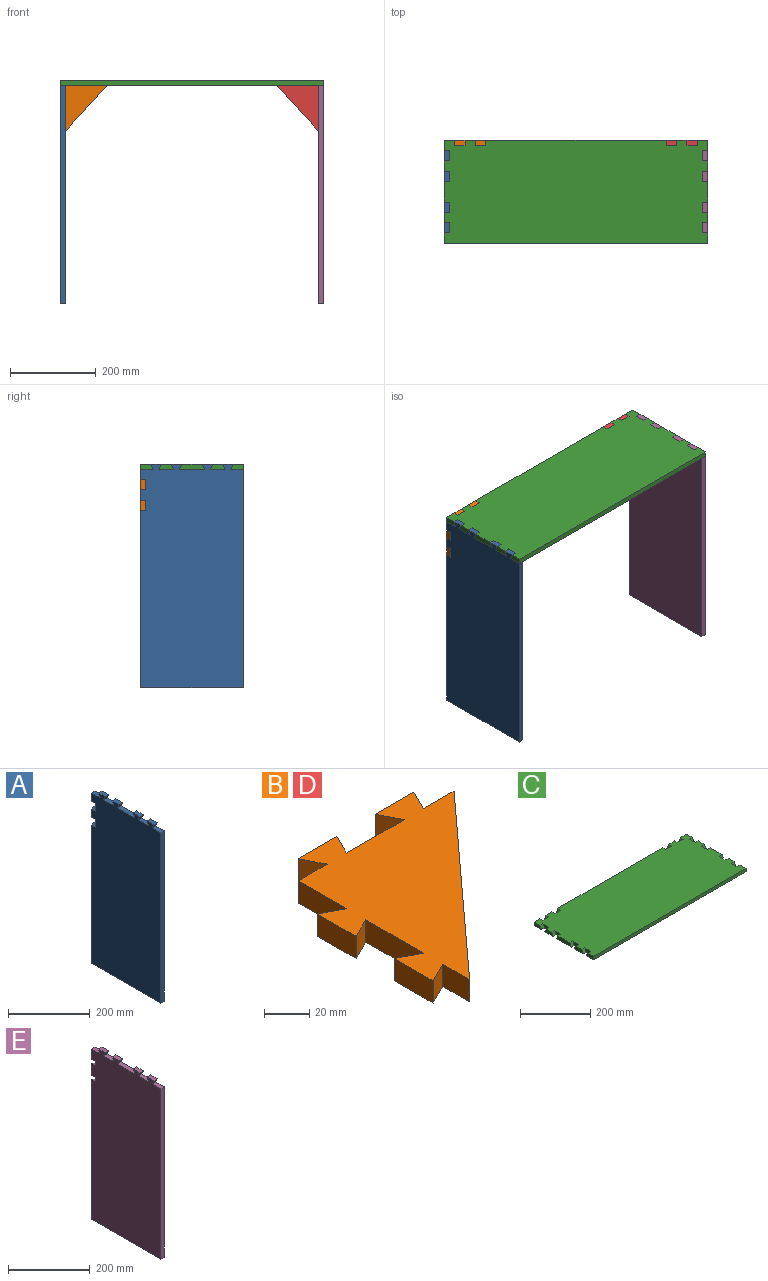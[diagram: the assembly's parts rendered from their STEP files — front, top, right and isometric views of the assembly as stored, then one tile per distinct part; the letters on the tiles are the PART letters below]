
ASSEMBLY  parts=5 mates=4
PART A: 30 faces, bbox 12x240x522 mm
  f0: plane 24x12mm, normal (0,1,0), area 216mm2, adj f24,f25,f28,f29
  f1: plane 24x12mm, normal (0,1,0), area 216mm2, adj f24,f25,f26,f27
  f2: plane 36x12mm, normal (0,0,1), area 432mm2, adj f3,f23,f24,f25
  f3: plane 12x12mm, normal (0,0.89,-0.45), area 161mm2, adj f2,f4,f24,f25
  f4: plane 24x12mm, normal (0,0,1), area 288mm2, adj f3,f5,f24,f25
  f5: plane 12x12mm, normal (0,-0.89,-0.45), area 161mm2, adj f4,f6,f24,f25
  f6: plane 30x12mm, normal (0,0,1), area 360mm2, adj f5,f7,f24,f25
  f7: plane 510x12mm, normal (0,-1,0), area 6120mm2, adj f6,f8,f24,f25
  f8: plane 240x12mm, normal (0,0,-1), area 2880mm2, adj f7,f9,f24,f25
  f9: plane 420x12mm, normal (0,1,0), area 5004mm2, adj f8,f24,f25,f29
  f10: plane 36x12mm, normal (0,1,0), area 360mm2, adj f24,f25,f27,f28
  f11: plane 30x12mm, normal (0,1,0), area 324mm2, adj f12,f24,f25,f26
  f12: plane 30x12mm, normal (0,0,1), area 360mm2, adj f11,f13,f24,f25
  f13: plane 12x12mm, normal (0,0.89,-0.45), area 161mm2, adj f12,f14,f24,f25
  f14: plane 24x12mm, normal (0,0,1), area 288mm2, adj f13,f15,f24,f25
  f15: plane 12x12mm, normal (0,-0.89,-0.45), area 161mm2, adj f14,f16,f24,f25
  f16: plane 36x12mm, normal (0,0,1), area 432mm2, adj f15,f17,f24,f25
  f17: plane 12x12mm, normal (0,0.89,-0.45), area 161mm2, adj f16,f18,f24,f25
  f18: plane 24x12mm, normal (0,0,1), area 288mm2, adj f17,f19,f24,f25
  f19: plane 12x12mm, normal (0,-0.89,-0.45), area 161mm2, adj f18,f20,f24,f25
  f20: plane 60x12mm, normal (0,0,1), area 720mm2, adj f19,f21,f24,f25
  f21: plane 12x12mm, normal (0,0.89,-0.45), area 161mm2, adj f20,f22,f24,f25
  f22: plane 24x12mm, normal (0,0,1), area 288mm2, adj f21,f23,f24,f25
  f23: plane 12x12mm, normal (0,-0.89,-0.45), area 161mm2, adj f2,f22,f24,f25
  f24: plane 522x240mm, normal (1,0,0), area 122976mm2, adj f0,f1,f2,f3,f4,f5,f6,f7
  f25: plane 522x240mm, normal (-1,0,0), area 122688mm2, adj f0,f1,f2,f3,f4,f5,f6,f7
  f26: plane 12x12mm, normal (-0.45,0,-0.89), area 161mm2, adj f1,f11,f24,f25
  f27: plane 12x12mm, normal (-0.45,0,0.89), area 161mm2, adj f1,f10,f24,f25
  f28: plane 12x12mm, normal (-0.45,0,-0.89), area 161mm2, adj f0,f10,f24,f25
  f29: plane 12x12mm, normal (-0.45,0,0.89), area 161mm2, adj f0,f9,f24,f25
PART B: 21 faces, bbox 109.1x118.8x12 mm
  f0: plane 16.8x12mm, normal (-1,0,0), area 201.6mm2, adj f1,f18,f19,f20
  f1: plane 106.8x97.09mm, normal (0.74,-0.67,0), area 1732mm2, adj f0,f2,f19,f20
  f2: plane 19.09x12mm, normal (0,1,0), area 229.1mm2, adj f1,f3,f19,f20
  f3: plane 12x12mm, normal (0.89,-0.45,0), area 161mm2, adj f2,f4,f19,f20
  f4: plane 24x12mm, normal (0,1,0), area 288mm2, adj f3,f5,f19,f20
  f5: plane 12x12mm, normal (-0.89,-0.45,0), area 161mm2, adj f4,f6,f19,f20
  f6: plane 36x12mm, normal (0,1,0), area 432mm2, adj f5,f7,f19,f20
  f7: plane 12x12mm, normal (0.89,-0.45,0), area 161mm2, adj f6,f8,f19,f20
  f8: plane 24x12mm, normal (0,1,0), area 288mm2, adj f7,f9,f19,f20
  f9: plane 12x12mm, normal (-0.89,-0.45,0), area 161mm2, adj f8,f10,f19,f20
  f10: plane 18x12mm, normal (0,1,0), area 216mm2, adj f9,f11,f19,f20
  f11: plane 30x12mm, normal (-1,0,0), area 360mm2, adj f10,f12,f19,f20
  f12: plane 12x12mm, normal (0.45,0.89,0), area 161mm2, adj f11,f13,f19,f20
  f13: plane 24x12mm, normal (-1,0,0), area 288mm2, adj f12,f14,f19,f20
  f14: plane 12x12mm, normal (0.45,-0.89,0), area 161mm2, adj f13,f15,f19,f20
  f15: plane 36x12mm, normal (-1,0,0), area 432mm2, adj f14,f16,f19,f20
  f16: plane 12x12mm, normal (0.45,0.89,0), area 161mm2, adj f15,f17,f19,f20
  f17: plane 24x12mm, normal (-1,0,0), area 288mm2, adj f16,f18,f19,f20
  f18: plane 12x12mm, normal (0.45,-0.89,0), area 161mm2, adj f0,f17,f19,f20
  f19: plane 118.8x109.09mm, normal (0,0,1), area 6048.7mm2, adj f0,f1,f2,f3,f4,f5,f6,f7
  f20: plane 118.8x109.09mm, normal (0,0,-1), area 6048.7mm2, adj f0,f1,f2,f3,f4,f5,f6,f7
PART C: 54 faces, bbox 614x240x12 mm
  f0: plane 24x12mm, normal (0,1,0), area 216mm2, adj f28,f29,f52,f53
  f1: plane 24x12mm, normal (0,1,0), area 216mm2, adj f28,f29,f50,f51
  f2: plane 24x12mm, normal (0,1,0), area 216mm2, adj f28,f29,f48,f49
  f3: plane 24x12mm, normal (0,1,0), area 216mm2, adj f28,f29,f46,f47
  f4: plane 24x12mm, normal (1,0,0), area 216mm2, adj f28,f29,f44,f45
  f5: plane 24x12mm, normal (1,0,0), area 216mm2, adj f28,f29,f42,f43
  f6: plane 24x12mm, normal (-1,0,0), area 216mm2, adj f28,f29,f32,f33
  f7: plane 24x12mm, normal (-1,0,0), area 216mm2, adj f28,f29,f30,f31
  f8: plane 36x12mm, normal (1,0,0), area 360mm2, adj f28,f29,f43,f44
  f9: plane 30x12mm, normal (1,0,0), area 324mm2, adj f10,f28,f29,f45
  f10: plane 30x12mm, normal (0,1,0), area 324mm2, adj f9,f28,f29,f46
  f11: plane 36x12mm, normal (0,1,0), area 360mm2, adj f28,f29,f47,f48
  f12: plane 434x12mm, normal (0,1,0), area 5136mm2, adj f28,f29,f49,f50
  f13: plane 36x12mm, normal (0,1,0), area 360mm2, adj f28,f29,f51,f52
  f14: plane 30x12mm, normal (0,1,0), area 324mm2, adj f15,f28,f29,f53
  f15: plane 30x12mm, normal (-1,0,0), area 324mm2, adj f14,f28,f29,f36
  f16: plane 24x12mm, normal (-1,0,0), area 216mm2, adj f28,f29,f36,f37
  f17: plane 36x12mm, normal (-1,0,0), area 360mm2, adj f28,f29,f34,f37
  f18: plane 24x12mm, normal (-1,0,0), area 216mm2, adj f28,f29,f34,f35
  f19: plane 60x12mm, normal (-1,0,0), area 648mm2, adj f28,f29,f32,f35
  f20: plane 36x12mm, normal (-1,0,0), area 360mm2, adj f28,f29,f30,f33
  f21: plane 30x12mm, normal (-1,0,0), area 324mm2, adj f22,f28,f29,f31
  f22: plane 614x12mm, normal (0,-1,0), area 7368mm2, adj f21,f23,f28,f29
  f23: plane 30x12mm, normal (1,0,0), area 324mm2, adj f22,f28,f29,f38
  f24: plane 24x12mm, normal (1,0,0), area 216mm2, adj f28,f29,f38,f39
  f25: plane 36x12mm, normal (1,0,0), area 360mm2, adj f28,f29,f39,f40
  f26: plane 24x12mm, normal (1,0,0), area 216mm2, adj f28,f29,f40,f41
  f27: plane 60x12mm, normal (1,0,0), area 648mm2, adj f28,f29,f41,f42
  f28: plane 614x240mm, normal (0,0,1), area 143904mm2, adj f0,f1,f2,f3,f4,f5,f6,f7
  f29: plane 614x240mm, normal (0,0,-1), area 145632mm2, adj f0,f1,f2,f3,f4,f5,f6,f7
  f30: plane 12x12mm, normal (0,-0.89,0.45), area 161mm2, adj f7,f20,f28,f29
  f31: plane 12x12mm, normal (0,0.89,0.45), area 161mm2, adj f7,f21,f28,f29
  f32: plane 12x12mm, normal (0,-0.89,0.45), area 161mm2, adj f6,f19,f28,f29
  f33: plane 12x12mm, normal (0,0.89,0.45), area 161mm2, adj f6,f20,f28,f29
  f34: plane 12x12mm, normal (0,-0.89,0.45), area 161mm2, adj f17,f18,f28,f29
  f35: plane 12x12mm, normal (0,0.89,0.45), area 161mm2, adj f18,f19,f28,f29
  f36: plane 12x12mm, normal (0,-0.89,0.45), area 161mm2, adj f15,f16,f28,f29
  f37: plane 12x12mm, normal (0,0.89,0.45), area 161mm2, adj f16,f17,f28,f29
  f38: plane 12x12mm, normal (0,0.89,0.45), area 161mm2, adj f23,f24,f28,f29
  f39: plane 12x12mm, normal (0,-0.89,0.45), area 161mm2, adj f24,f25,f28,f29
  f40: plane 12x12mm, normal (0,0.89,0.45), area 161mm2, adj f25,f26,f28,f29
  f41: plane 12x12mm, normal (0,-0.89,0.45), area 161mm2, adj f26,f27,f28,f29
  f42: plane 12x12mm, normal (0,0.89,0.45), area 161mm2, adj f5,f27,f28,f29
  f43: plane 12x12mm, normal (0,-0.89,0.45), area 161mm2, adj f5,f8,f28,f29
  f44: plane 12x12mm, normal (0,0.89,0.45), area 161mm2, adj f4,f8,f28,f29
  f45: plane 12x12mm, normal (0,-0.89,0.45), area 161mm2, adj f4,f9,f28,f29
  f46: plane 12x12mm, normal (-0.89,0,0.45), area 161mm2, adj f3,f10,f28,f29
  f47: plane 12x12mm, normal (0.89,0,0.45), area 161mm2, adj f3,f11,f28,f29
  f48: plane 12x12mm, normal (-0.89,0,0.45), area 161mm2, adj f2,f11,f28,f29
  f49: plane 12x12mm, normal (0.89,0,0.45), area 161mm2, adj f2,f12,f28,f29
  f50: plane 12x12mm, normal (-0.89,0,0.45), area 161mm2, adj f1,f12,f28,f29
  f51: plane 12x12mm, normal (0.89,0,0.45), area 161mm2, adj f1,f13,f28,f29
  f52: plane 12x12mm, normal (-0.89,0,0.45), area 161mm2, adj f0,f13,f28,f29
  f53: plane 12x12mm, normal (0.89,0,0.45), area 161mm2, adj f0,f14,f28,f29
PART D: same geometry as B
PART E: 30 faces, bbox 12x240x522 mm
  f0: plane 24x12mm, normal (0,1,0), area 216mm2, adj f24,f25,f28,f29
  f1: plane 24x12mm, normal (0,1,0), area 216mm2, adj f24,f25,f26,f27
  f2: plane 36x12mm, normal (0,0,1), area 432mm2, adj f3,f23,f24,f25
  f3: plane 12x12mm, normal (0,0.89,-0.45), area 161mm2, adj f2,f4,f24,f25
  f4: plane 24x12mm, normal (0,0,1), area 288mm2, adj f3,f5,f24,f25
  f5: plane 12x12mm, normal (0,-0.89,-0.45), area 161mm2, adj f4,f6,f24,f25
  f6: plane 30x12mm, normal (0,0,1), area 360mm2, adj f5,f7,f24,f25
  f7: plane 510x12mm, normal (0,-1,0), area 6120mm2, adj f6,f8,f24,f25
  f8: plane 240x12mm, normal (0,0,-1), area 2880mm2, adj f7,f9,f24,f25
  f9: plane 420x12mm, normal (0,1,0), area 5004mm2, adj f8,f24,f25,f29
  f10: plane 36x12mm, normal (0,1,0), area 360mm2, adj f24,f25,f27,f28
  f11: plane 30x12mm, normal (0,1,0), area 324mm2, adj f12,f24,f25,f26
  f12: plane 30x12mm, normal (0,0,1), area 360mm2, adj f11,f13,f24,f25
  f13: plane 12x12mm, normal (0,0.89,-0.45), area 161mm2, adj f12,f14,f24,f25
  f14: plane 24x12mm, normal (0,0,1), area 288mm2, adj f13,f15,f24,f25
  f15: plane 12x12mm, normal (0,-0.89,-0.45), area 161mm2, adj f14,f16,f24,f25
  f16: plane 36x12mm, normal (0,0,1), area 432mm2, adj f15,f17,f24,f25
  f17: plane 12x12mm, normal (0,0.89,-0.45), area 161mm2, adj f16,f18,f24,f25
  f18: plane 24x12mm, normal (0,0,1), area 288mm2, adj f17,f19,f24,f25
  f19: plane 12x12mm, normal (0,-0.89,-0.45), area 161mm2, adj f18,f20,f24,f25
  f20: plane 60x12mm, normal (0,0,1), area 720mm2, adj f19,f21,f24,f25
  f21: plane 12x12mm, normal (0,0.89,-0.45), area 161mm2, adj f20,f22,f24,f25
  f22: plane 24x12mm, normal (0,0,1), area 288mm2, adj f21,f23,f24,f25
  f23: plane 12x12mm, normal (0,-0.89,-0.45), area 161mm2, adj f2,f22,f24,f25
  f24: plane 522x240mm, normal (1,0,0), area 122688mm2, adj f0,f1,f2,f3,f4,f5,f6,f7
  f25: plane 522x240mm, normal (-1,0,0), area 122976mm2, adj f0,f1,f2,f3,f4,f5,f6,f7
  f26: plane 12x12mm, normal (0.45,0,-0.89), area 161mm2, adj f1,f11,f24,f25
  f27: plane 12x12mm, normal (0.45,0,0.89), area 161mm2, adj f1,f10,f24,f25
  f28: plane 12x12mm, normal (0.45,0,-0.89), area 161mm2, adj f0,f10,f24,f25
  f29: plane 12x12mm, normal (0.45,0,0.89), area 161mm2, adj f0,f9,f24,f25
PLACE A t=(-354.41,7.9,-140.02)mm
PLACE B rot(axis=(1,0,0),90deg) t=(-95.79,127.9,-126.03)mm
PLACE C t=(-47.41,7.9,108.98)mm fixed
PLACE D rot(axis=(0,0.71,0.71),180deg) t=(0.97,115.9,-126.03)mm
PLACE E t=(247.59,7.9,-140.02)mm
MATE slider A.f25 <-> C.f20  axis (-1,0,0) through (-354.41,-64.1,120.98)mm
MATE slider D.f19 <-> C.f10  axis (0,1,0) through (235.59,127.9,120.98)mm
MATE slider E.f24 <-> C.f9  axis (1,0,0) through (259.59,103.9,120.98)mm
MATE slider B.f20 <-> C.f14  axis (0,1,0) through (-330.41,127.9,120.98)mm
